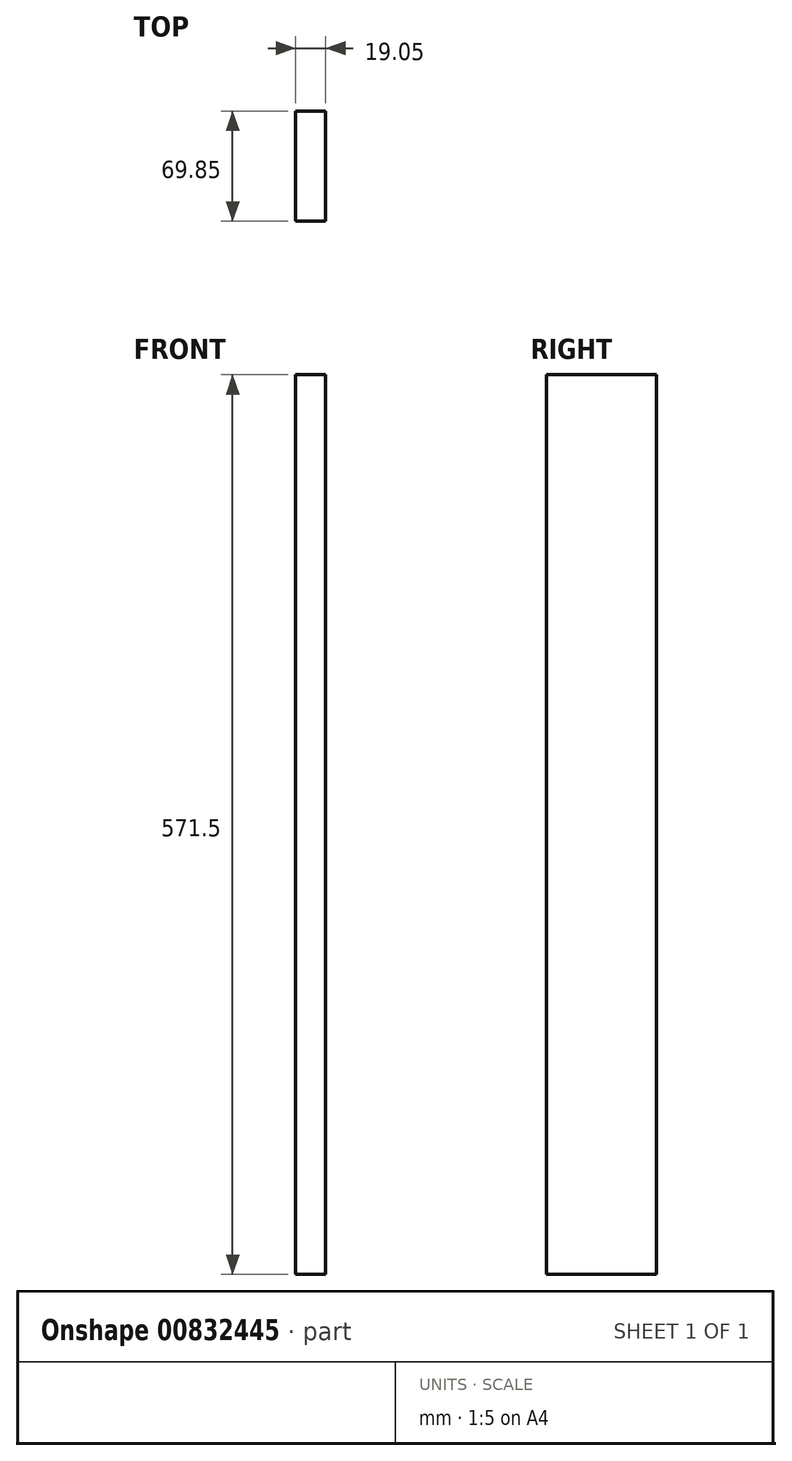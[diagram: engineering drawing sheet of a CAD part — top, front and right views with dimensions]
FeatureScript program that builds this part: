
annotation { "Feature Type Name" : "Feature", "Feature Type Description" : "" }
export const myFeature = defineFeature(function(context is Context, id is Id, definition is map)
    precondition{}
    {
        {
            var Q0;
            Q0=qCreatedBy(makeId("Front.planeOp"),FACE);
            var sketch = newSketch(context, id + "F0", { "sketchPlane" : qUnion([Q0])});
            skLineSegment(sketch, "E0.bottom", {"start": v(-21.96, 286.32) * mm, "end": v(-2.91, 286.32) * mm});
            skLineSegment(sketch, "E0.top", {"start": v(-21.96, -285.18) * mm, "end": v(-2.91, -285.18) * mm});
            skLineSegment(sketch, "E0.left", {"start": v(-21.96, 286.32) * mm, "end": v(-21.96, -285.18) * mm});
            skLineSegment(sketch, "E0.right", {"start": v(-2.91, 286.32) * mm, "end": v(-2.91, -285.18) * mm});
            skSolve(sketch);
        }
        {
            var Q0;
            Q0=sQuery(id+"F0.wireOp",EDGE,"E0.bottom");
            var Q1;
            Q1=sQuery(id+"F0.wireOp",EDGE,"E0.right");
            var Q2;
            Q2=sQuery(id+"F0.wireOp",EDGE,"E0.left");
            var Q3;
            Q3=sQuery(id+"F0.wireOp",EDGE,"E0.top");
            extrude(context, id + "F1", {"bodyType" : ToolBodyType.SURFACE, "surfaceEntities" : qUnion([Q0, Q1, Q2, Q3]), "depth" : 69.85 * mm, "offsetDistance" : 25.4 * mm});
        }
    });
